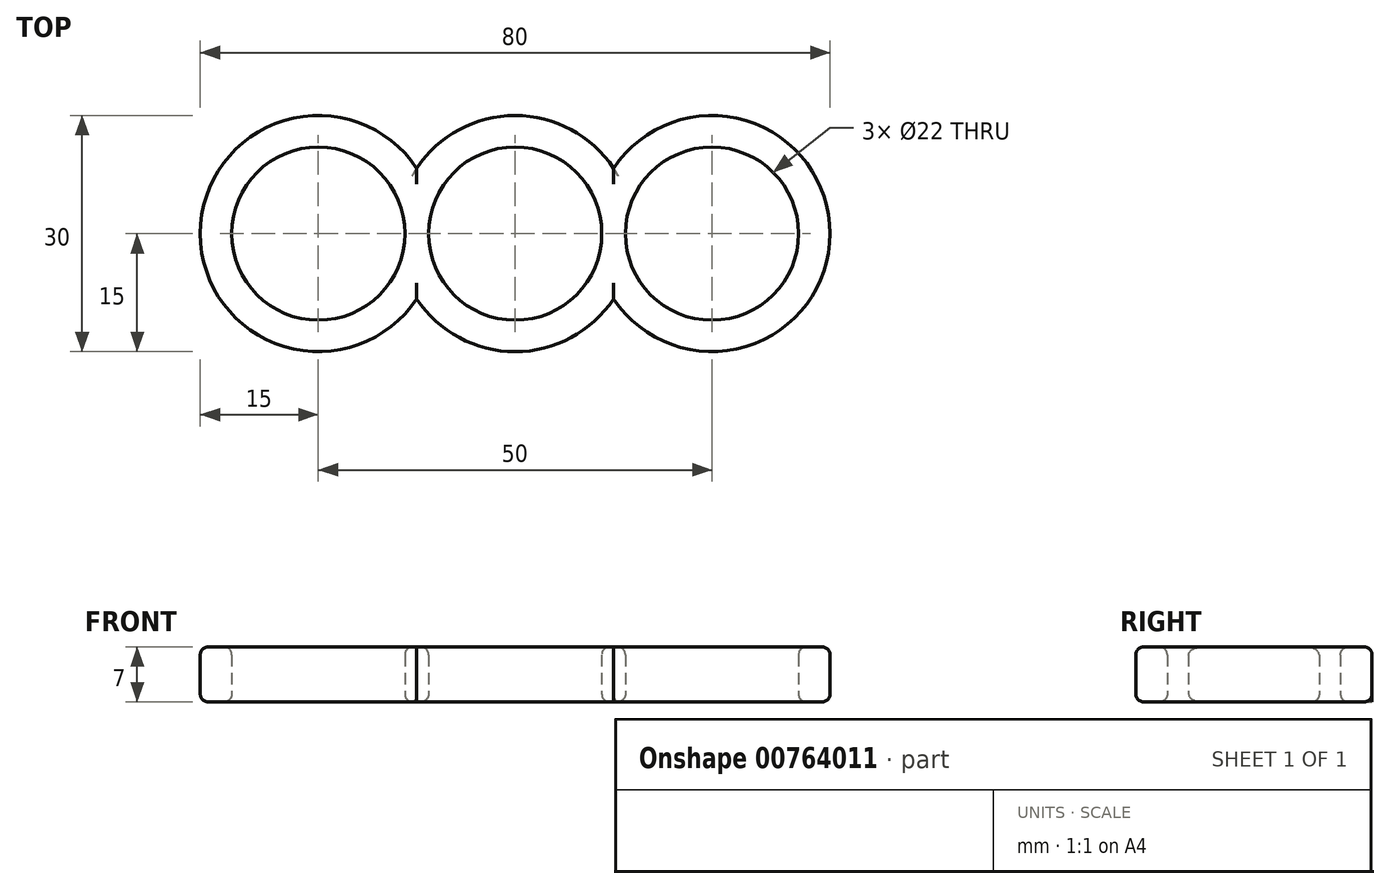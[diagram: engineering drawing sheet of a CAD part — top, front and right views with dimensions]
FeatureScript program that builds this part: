
annotation { "Feature Type Name" : "Feature", "Feature Type Description" : "" }
export const myFeature = defineFeature(function(context is Context, id is Id, definition is map)
    precondition{}
    {
        {
            var Q0;
            Q0=qCreatedBy(makeId("Top.planeOp"),FACE);
            var sketch = newSketch(context, id + "F0", { "sketchPlane" : qUnion([Q0])});
            skArc(sketch, "E0", {"start": v(0, 11) * mm, "mid": v(-11, 0) * mm, "end": v(0, -11) * mm});
            skArc(sketch, "E1", {"start": v(-12.5, -8.3) * mm, "mid": v(-7.1, -13.22) * mm, "end": v(0, -15) * mm});
            skCircle(sketch, "E2", {"center": v(-25, 0) * mm, "radius": 11 * mm});
            skArc(sketch, "E3", {"start": v(-12.5, 8.3) * mm, "mid": v(-40, 0) * mm, "end": v(-12.5, -8.3) * mm});
            skArc(sketch, "E4.trimOffspring", {"start": v(0, 15) * mm, "mid": v(-7.1, 13.22) * mm, "end": v(-12.5, 8.3) * mm});
            skArc(sketch, "E5.MirrorCS", {"start": v(12.5, 8.3) * mm, "mid": v(40, 0) * mm, "end": v(12.5, -8.3) * mm});
            skArc(sketch, "E6.MirrorCS", {"start": v(0, 11) * mm, "mid": v(11, 0) * mm, "end": v(0, -11) * mm});
            skCircle(sketch, "E7.MirrorC", {"center": v(25, 0) * mm, "radius": 11 * mm});
            skArc(sketch, "E8.MirrorCS", {"start": v(12.5, -8.3) * mm, "mid": v(7.1, -13.22) * mm, "end": v(0, -15) * mm});
            skArc(sketch, "E9.MirrorCS", {"start": v(0, 15) * mm, "mid": v(7.1, 13.22) * mm, "end": v(12.5, 8.3) * mm});
            skSolve(sketch);
        }
        {
            var Q0;
            Q0 = qSketchRegion(id + "F0", true);
            extrude(context, id + "F1", {"entities" : qUnion([Q0]), "depth" : 7 * mm, "offsetDistance" : 25 * mm});
        }
        {
            var Q0;
            Q0=makeQuery(id+"F1.opExtrude","CAP_EDGE",EDGE,{"disambiguationData":[OSD([sQuery(id+"F0.wireOp",EDGE,"E3")])],"isStart":false});
            var Q1;
            Q1=makeQuery(id+"F1.opExtrude","CAP_EDGE",EDGE,{"disambiguationData":[OSD([sQuery(id+"F0.wireOp",EDGE,"E2")])],"isStart":false});
            var Q2;
            Q2=makeQuery(id+"F1.opExtrude","CAP_EDGE",EDGE,{"disambiguationData":[OSD([sQuery(id+"F0.wireOp",EDGE,"E4.trimOffspring"),sQuery(id+"F0.wireOp",EDGE,"E9.MirrorCS")])],"isStart":false});
            var Q3;
            Q3=makeQuery(id+"F1.opExtrude","CAP_EDGE",EDGE,{"disambiguationData":[OSD([sQuery(id+"F0.wireOp",EDGE,"E0"),sQuery(id+"F0.wireOp",EDGE,"E6.MirrorCS")])],"isStart":false});
            var Q4;
            Q4=makeQuery(id+"F1.opExtrude","CAP_EDGE",EDGE,{"disambiguationData":[OSD([sQuery(id+"F0.wireOp",EDGE,"E5.MirrorCS")])],"isStart":false});
            var Q5;
            Q5=makeQuery(id+"F1.opExtrude","CAP_EDGE",EDGE,{"disambiguationData":[OSD([sQuery(id+"F0.wireOp",EDGE,"E7.MirrorC")])],"isStart":false});
            var Q6;
            Q6=makeQuery(id+"F1.opExtrude","CAP_EDGE",EDGE,{"disambiguationData":[OSD([sQuery(id+"F0.wireOp",EDGE,"E1"),sQuery(id+"F0.wireOp",EDGE,"E8.MirrorCS")])],"isStart":false});
            var Q7;
            Q7=makeQuery(id+"F1.opExtrude","CAP_EDGE",EDGE,{"disambiguationData":[OSD([sQuery(id+"F0.wireOp",EDGE,"E5.MirrorCS")])],"isStart":true});
            var Q8;
            Q8=makeQuery(id+"F1.opExtrude","CAP_EDGE",EDGE,{"disambiguationData":[OSD([sQuery(id+"F0.wireOp",EDGE,"E1"),sQuery(id+"F0.wireOp",EDGE,"E8.MirrorCS")])],"isStart":true});
            var Q9;
            Q9=makeQuery(id+"F1.opExtrude","CAP_EDGE",EDGE,{"disambiguationData":[OSD([sQuery(id+"F0.wireOp",EDGE,"E3")])],"isStart":true});
            var Q10;
            Q10=makeQuery(id+"F1.opExtrude","CAP_EDGE",EDGE,{"disambiguationData":[OSD([sQuery(id+"F0.wireOp",EDGE,"E2")])],"isStart":true});
            var Q11;
            Q11=makeQuery(id+"F1.opExtrude","CAP_EDGE",EDGE,{"disambiguationData":[OSD([sQuery(id+"F0.wireOp",EDGE,"E0"),sQuery(id+"F0.wireOp",EDGE,"E6.MirrorCS")])],"isStart":true});
            var Q12;
            Q12=makeQuery(id+"F1.opExtrude","CAP_EDGE",EDGE,{"disambiguationData":[OSD([sQuery(id+"F0.wireOp",EDGE,"E7.MirrorC")])],"isStart":true});
            fillet(context, id + "F2", {"entities" : qUnion([Q0, Q1, Q2, Q3, Q4, Q5, Q6, Q7, Q8, Q9, Q10, Q11, Q12]), "radius" : 1 * mm, "tangentPropagation" : true, "allowEdgeOverflow" : false});
        }
    });
